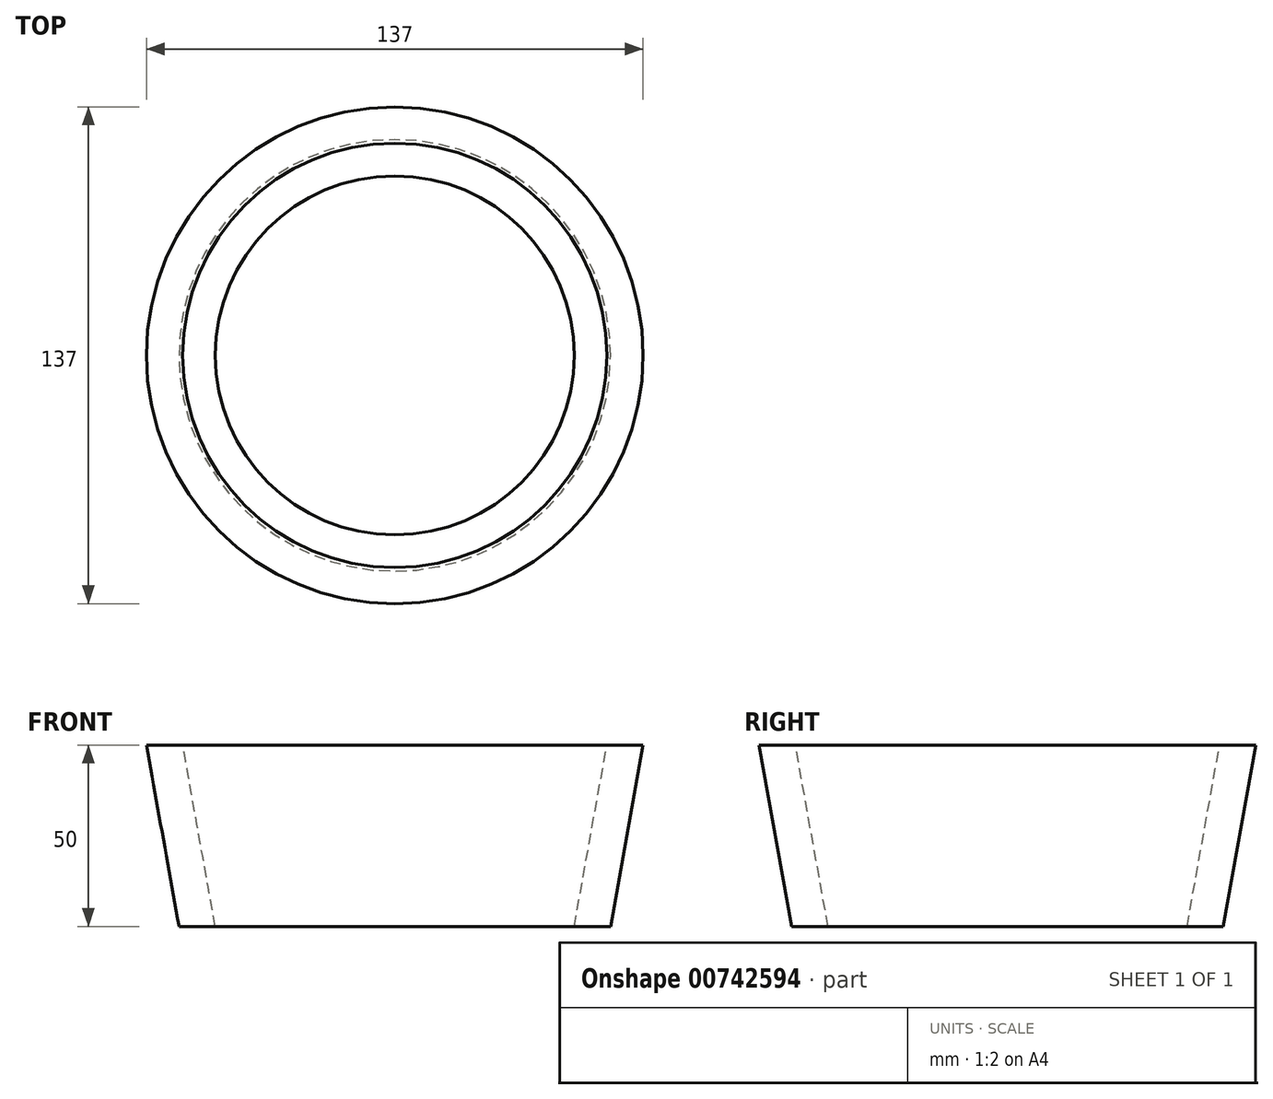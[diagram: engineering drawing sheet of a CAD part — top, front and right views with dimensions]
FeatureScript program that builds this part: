
annotation { "Feature Type Name" : "Feature", "Feature Type Description" : "" }
export const myFeature = defineFeature(function(context is Context, id is Id, definition is map)
    precondition{}
    {
        {
            var Q0;
            Q0=qCreatedBy(makeId("Front.planeOp"),FACE);
            var sketch = newSketch(context, id + "F0", { "sketchPlane" : qUnion([Q0])});
            skLineSegment(sketch, "E0", {"start": v(0, 0) * mm, "end": v(0, 50) * mm, "construction": true});
            skLineSegment(sketch, "E1", {"start": v(-68.5, 50) * mm, "end": v(-59.5, 0) * mm});
            skLineSegment(sketch, "E2", {"start": v(-59.5, 0) * mm, "end": v(-49.5, 0) * mm});
            skLineSegment(sketch, "E3", {"start": v(-49.5, 0) * mm, "end": v(-58.5, 50) * mm});
            skLineSegment(sketch, "E4", {"start": v(-68.5, 50) * mm, "end": v(-58.5, 50) * mm});
            skLineSegment(sketch, "E5", {"start": v(-58.5, 50) * mm, "end": v(0, 50) * mm, "construction": true});
            skSolve(sketch);
        }
        {
            var Q0;
            Q0=makeQuery(id+"F0.imprint","IMPRINT",FACE,{"disambiguationData":[TD([[makeQuery(id+"F0.imprint","IMPRINT",EDGE,{"derivedFrom":sQuery(id+"F0.wireOp",EDGE,"E1")}),1.0]])]});
            var Q1;
            Q1=sQuery(id+"F0.wireOp",EDGE,"E0");
            revolve(context, id + "F1", {"surfaceOperationType" : NewSurfaceOperationType.NEW, "entities" : qUnion([Q0]), "axis" : qUnion([Q1]), "revolveType" : RevolveType.FULL});
        }
    });
